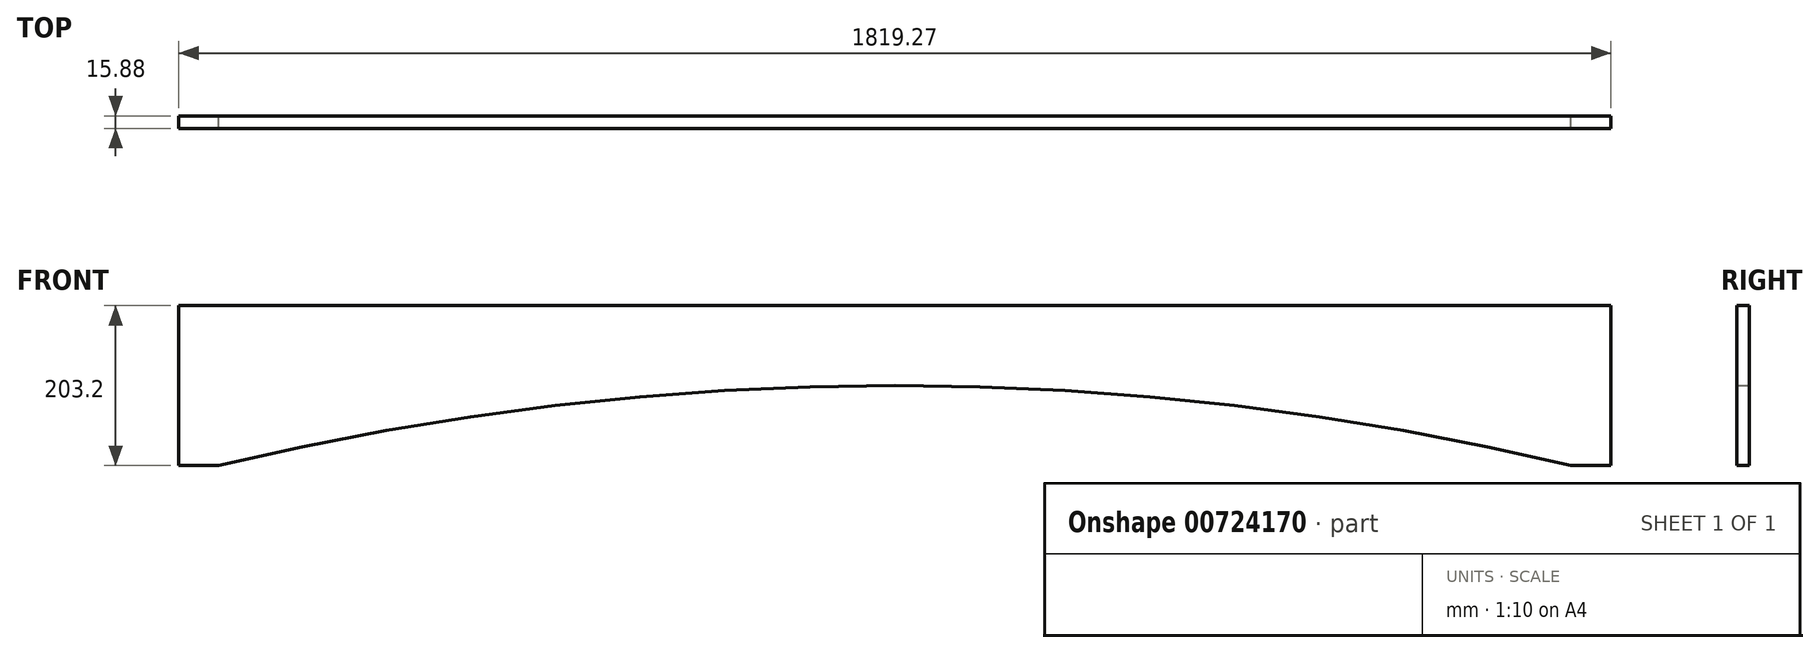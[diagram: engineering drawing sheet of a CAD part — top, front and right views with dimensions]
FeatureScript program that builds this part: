
annotation { "Feature Type Name" : "Feature", "Feature Type Description" : "" }
export const myFeature = defineFeature(function(context is Context, id is Id, definition is map)
    precondition{}
    {
        {
            var Q0;
            Q0=qCreatedBy(makeId("Front.planeOp"),FACE);
            var sketch = newSketch(context, id + "F0", { "sketchPlane" : qUnion([Q0])});
            skLineSegment(sketch, "E0", {"start": v(-70.81, 96) * mm, "end": v(1748.46, 96) * mm});
            skLineSegment(sketch, "E1", {"start": v(1748.46, 96) * mm, "end": v(1748.46, -107.2) * mm});
            skLineSegment(sketch, "E2", {"start": v(1748.46, -107.2) * mm, "end": v(1697.66, -107.2) * mm});
            skLineSegment(sketch, "E3", {"start": v(-70.81, 96) * mm, "end": v(-70.81, -107.2) * mm});
            skLineSegment(sketch, "E4", {"start": v(-70.81, -107.2) * mm, "end": v(-20.01, -107.2) * mm});
            skArc(sketch, "E5", {"start": v(1697.66, -107.2) * mm, "mid": v(838.82, -5.6) * mm, "end": v(-20.01, -107.2) * mm});
            skPoint(sketch, "E6.start.orphan", {"position": v(838.82, 96) * mm});
            skSolve(sketch);
        }
        {
            var Q0;
            Q0 = qSketchRegion(id + "F0", true);
            extrude(context, id + "F1", {"entities" : qUnion([Q0]), "depth" : 15.88 * mm, "offsetDistance" : 25.4 * mm});
        }
    });
